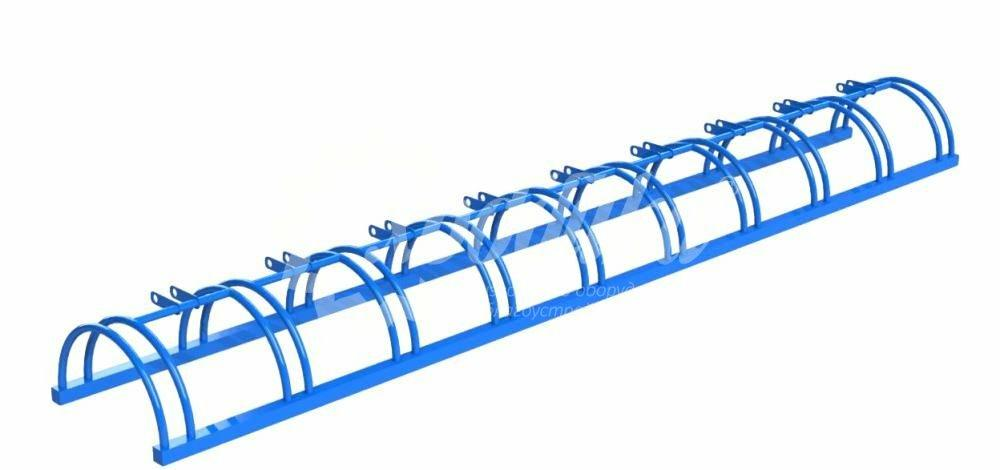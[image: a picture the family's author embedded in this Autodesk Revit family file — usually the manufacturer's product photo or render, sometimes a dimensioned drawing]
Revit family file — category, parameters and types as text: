
# Revit family: 13778 Парковка для самокатов VELO-19 Хоббика
name_source: partatom
category: Антураж
revit_build: Autodesk Revit 2018 (Build: 20180423_1000(x64)
units: mm (PartAtom-declared; Revit-internal decimal feet)

## family parameters
Всегда вертикально = Да
Источник визуального образа = Геометрия семейства
На основе рабочей плоскости = Нет
Общий = Нет
При загрузке вырезать с полостями = Нет
Точка расчета площади = Нет

## types (3) — shared parameters
URL = https://hobbyka.ru
Артикул товара = Арт. 13778
Высота = 350 мм
Группа модели = Велопарковки
Изготовитель = ООО «Хоббика»
Изображение типоразмера = Парковка для самокатов VELO-19 Арт 13778.jpg
Ширина = 400 мм

## per-type parameters (varying)
| type | Версия на 19 мест | Версия на 9 мест | Версия на 9 мест нержавеющая сталь | Длина | Кол-во мест | Материал изделия | Описание | Цвет каркаса |
| Версия на 19 мест | Да | Нет | Нет | 6110 мм | 19 | Сталь | Парковка для самокатов VELO-19. Версия «Профильная сталь 19 мест» | Нержавеющая сталь |
| Версия на 9 мест | Нет | Да | Нет | 2860 мм | 9 | Сталь | Парковка для самокатов VELO-19. Версия «Профильная сталь 9 мест» | Сталь |
| Версия на 9 мест нержавеющая сталь | Нет | Нет | Да | 2860 мм | 9 | Нержавеющая сталь | Парковка для самокатов VELO-19. Версия «Матовая нержавейка 9 мест» | Сталь |
